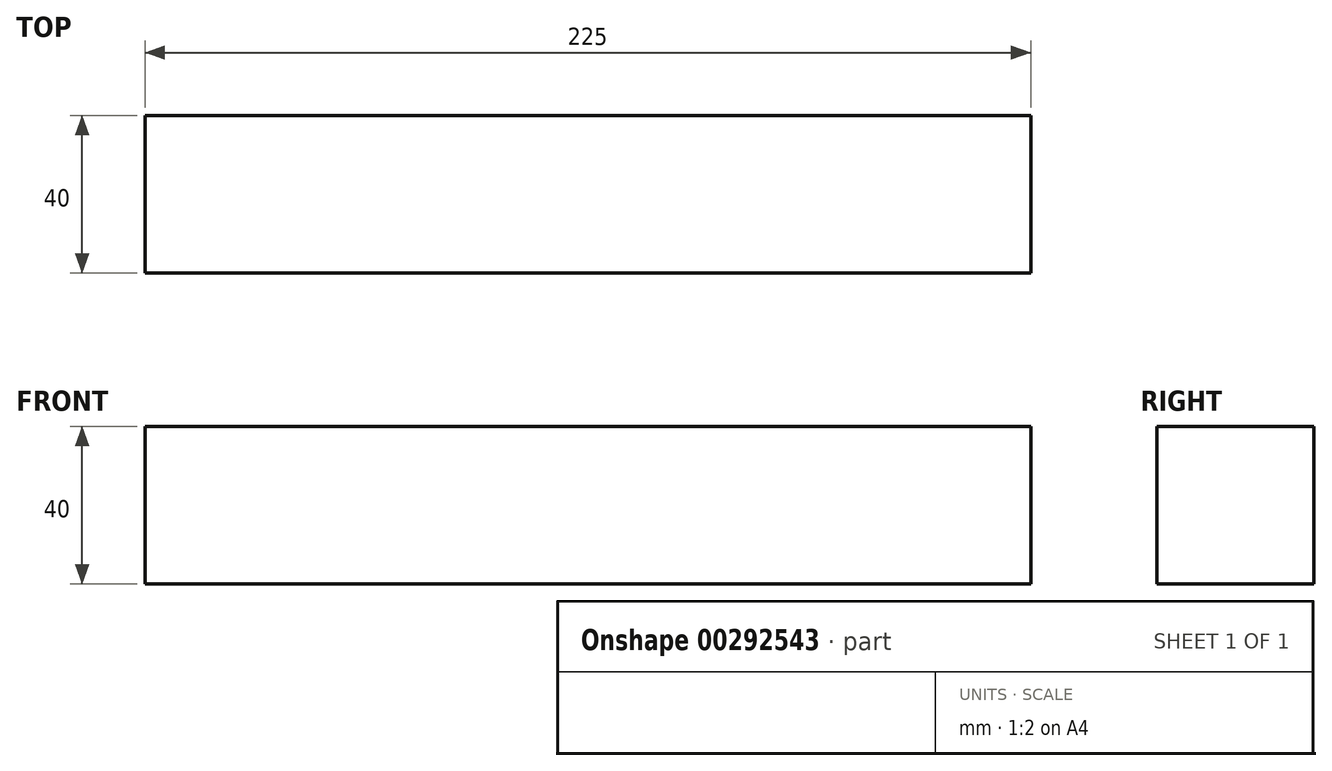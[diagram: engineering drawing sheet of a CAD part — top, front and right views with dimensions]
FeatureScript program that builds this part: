
annotation { "Feature Type Name" : "Feature", "Feature Type Description" : "" }
export const myFeature = defineFeature(function(context is Context, id is Id, definition is map)
    precondition{}
    {
        {
            var Q0;
            Q0=qCreatedBy(makeId("Front.planeOp"),FACE);
            var sketch = newSketch(context, id + "F0", { "sketchPlane" : qUnion([Q0])});
            skLineSegment(sketch, "E0.bottom", {"start": v(-112.24, 23.06) * mm, "end": v(112.76, 23.06) * mm});
            skLineSegment(sketch, "E0.top", {"start": v(-112.24, -16.94) * mm, "end": v(112.76, -16.94) * mm});
            skLineSegment(sketch, "E0.left", {"start": v(-112.24, 23.06) * mm, "end": v(-112.24, -16.94) * mm});
            skLineSegment(sketch, "E0.right", {"start": v(112.76, 23.06) * mm, "end": v(112.76, -16.94) * mm});
            skSolve(sketch);
        }
        {
            var Q0;
            Q0 = qSketchRegion(id + "F0", true);
            extrude(context, id + "F1", {"entities" : qUnion([Q0]), "depth" : 40 * mm});
        }
    });
